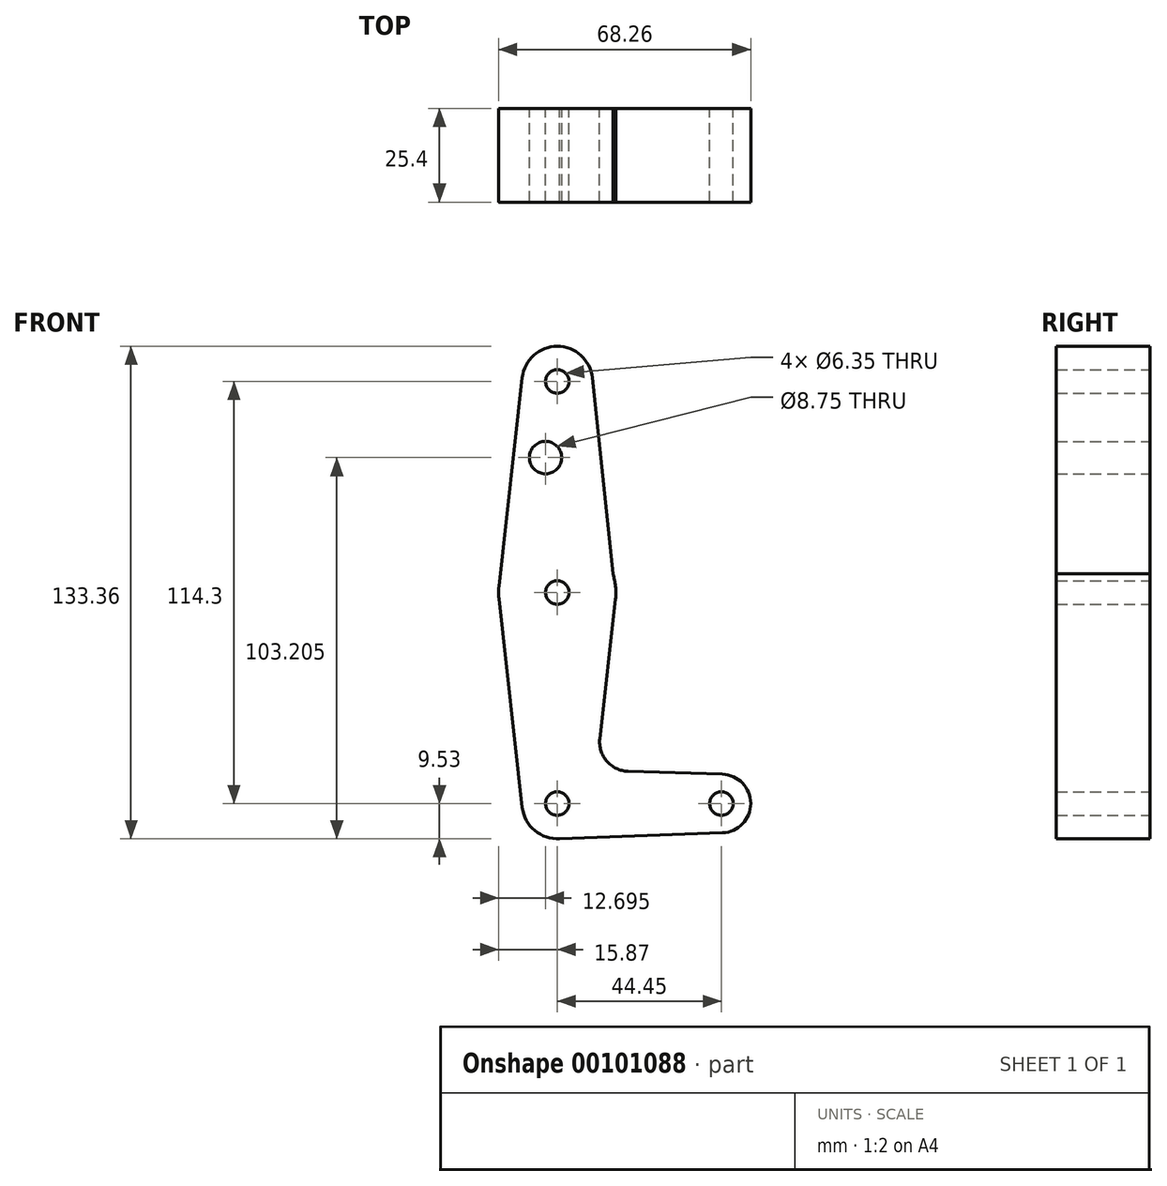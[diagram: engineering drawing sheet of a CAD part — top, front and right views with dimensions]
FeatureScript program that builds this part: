
annotation { "Feature Type Name" : "Feature", "Feature Type Description" : "" }
export const myFeature = defineFeature(function(context is Context, id is Id, definition is map)
    precondition{}
    {
        {
            var Q0;
            Q0=qCreatedBy(makeId("Front.planeOp"),FACE);
            var sketch = newSketch(context, id + "F0", { "sketchPlane" : qUnion([Q0])});
            skLineSegment(sketch, "E0", {"start": v(0, 0) * mm, "end": v(0, 114.3) * mm, "construction": true});
            skLineSegment(sketch, "E1", {"start": v(0, 114.3) * mm, "end": v(0, 0) * mm, "construction": true});
            skCircle(sketch, "E2", {"center": v(0, 114.3) * mm, "radius": 9.53 * mm});
            skCircle(sketch, "E3", {"center": v(0, 0) * mm, "radius": 9.53 * mm});
            skCircle(sketch, "E4", {"center": v(0, 57.15) * mm, "radius": 15.88 * mm});
            skCircle(sketch, "E5", {"center": v(44.45, 0) * mm, "radius": 7.94 * mm});
            skLineSegment(sketch, "E6", {"start": v(0, 0) * mm, "end": v(76.42, 0) * mm});
            skLineSegment(sketch, "E7", {"start": v(76.42, 0) * mm, "end": v(0, 0) * mm});
            skLineSegment(sketch, "E8", {"start": v(0, 0) * mm, "end": v(0, 78.14) * mm, "construction": true});
            skLineSegment(sketch, "E9", {"start": v(-9.47, 115.36) * mm, "end": v(-15.78, 58.91) * mm});
            skLineSegment(sketch, "E10", {"start": v(9.47, 115.3) * mm, "end": v(15.77, 55.37) * mm});
            skLineSegment(sketch, "E11", {"start": v(0, -9.53) * mm, "end": v(44.73, -7.93) * mm});
            skCircle(sketch, "E12", {"center": v(0, 57.15) * mm, "radius": 3.18 * mm});
            skCircle(sketch, "E13", {"center": v(0, 114.3) * mm, "radius": 3.18 * mm});
            skCircle(sketch, "E14", {"center": v(0, 0) * mm, "radius": 3.18 * mm});
            skCircle(sketch, "E15", {"center": v(44.45, 0) * mm, "radius": 3.18 * mm});
            skCircle(sketch, "E16", {"center": v(-3.18, 93.68) * mm, "radius": 4.38 * mm});
            skLineSegment(sketch, "E17", {"start": v(19.16, 8.73) * mm, "end": v(44.7, 7.93) * mm});
            skLineSegment(sketch, "E18", {"start": v(-15.78, 55.39) * mm, "end": v(-9.47, -1.06) * mm});
            skLineSegment(sketch, "E19", {"start": v(11.5, 17.57) * mm, "end": v(15.77, 55.37) * mm});
            skPoint(sketch, "E20.newPointA", {"position": v(9.53, 0) * mm});
            skArc(sketch, "E20.filletArc", {"start": v(11.5, 17.57) * mm, "mid": v(13.4, 11.48) * mm, "end": v(19.16, 8.73) * mm});
            skSolve(sketch);
        }
        {
            var Q0;
            Q0 = qSketchRegion(id + "F0", true);
            extrude(context, id + "F1", {"entities" : qUnion([Q0]), "depth" : 25.4 * mm});
        }
    });
